# Revit family: Furniture_Office-Chairs_Flokk_Giroflex-10
name_source: partatom
category: Furniture
units: mm (PartAtom-declared; Revit-internal decimal feet)

## family parameters
Always vertical = Yes
Cut with Voids When Loaded = No
OmniClass Number = 23.40.20.14.14.11
OmniClass Title = Chairs
Room Calculation Point = No
Shared = No
Work Plane-Based = No

## types (1)
- Giroflex 10
    AssetType = Movable
    BIMObjectName = Furniture_Office-Chairs_Flokk_Giroflex-10
    Brand = Flokk
    Category = Giroflex
    Color = Various
    Cost = 0 $
    Default Elevation = 0 mm  [stored 0 ft]
    Description = The giroflex 10 is an iconic and colourful object in itself. Yet, it is not just something for the eye but also for the whole locomotor system. The stand-up seating with the giroflex 10 fosters balance and strengthens the muscles, while relieving the spine and counteracting poor posture.

The 10 3020 version is delivered with a integral foam seat. One can also ad a covering cone in various cover materials and colours on option.
    Designer = Zemp + Partner Design, update by Paolo Fancelli.
    DurationUnit = Year
    Features = The 10 2020 version is delivered with a uphostered seat. One can also choose a cleanguard seat and a covering cone in various cover materials and colours on option.
    IfcExportAs = IfcFurnishingElementType
    IfcExportType = CHAIR
    LowestSeatingHeight = 740 mm  [stored 2.42782 ft]
    MainColor = Various
    Manufacturer = Flokk
    ManufacturerName = Flokk
    ManufacturerURL = https://www.flokk.com
    Material = Plastic, Metal and Textile
    Model = Giroflex 10
    ModelNumber = 10-2020
    NBSDescription = Stacking chairs
    NBSReference = 45-35-20/355
    Name = Giroflex-10
    NominalDepth = 330 mm
    NominalLength = 330 mm
    ProductDatasheet = https://flokkplatformprod.blob.core.windows.net
    ProductInformation = A clever concept for good dynamics. The innovative giroflex 10 sit-stand stool brings a new healthy dynamic to sitting.
    SeatingHeight = 740 mm  [stored 2.42782 ft]
    Shape = Sculptured
    Size = 330x330x740 mm
    URL = https://store.flokk.com
    Uniclass2 = Pr_40_50_12_51
    Uniclass2015Description = Meeting room chairs
    Uniclass2015Reference = Pr_40_50_12_51
    Version = 1
    VersionDate = 20/12/2022
    WarrantyDurationUnit = Year

note: [stored X ft] marks values corroborated as IEEE doubles in the binary element streams (Revit-internal decimal feet)

## geometry (parser evidence)
native form markers: Sweep x4
no freeform markers — native parametric forms only
